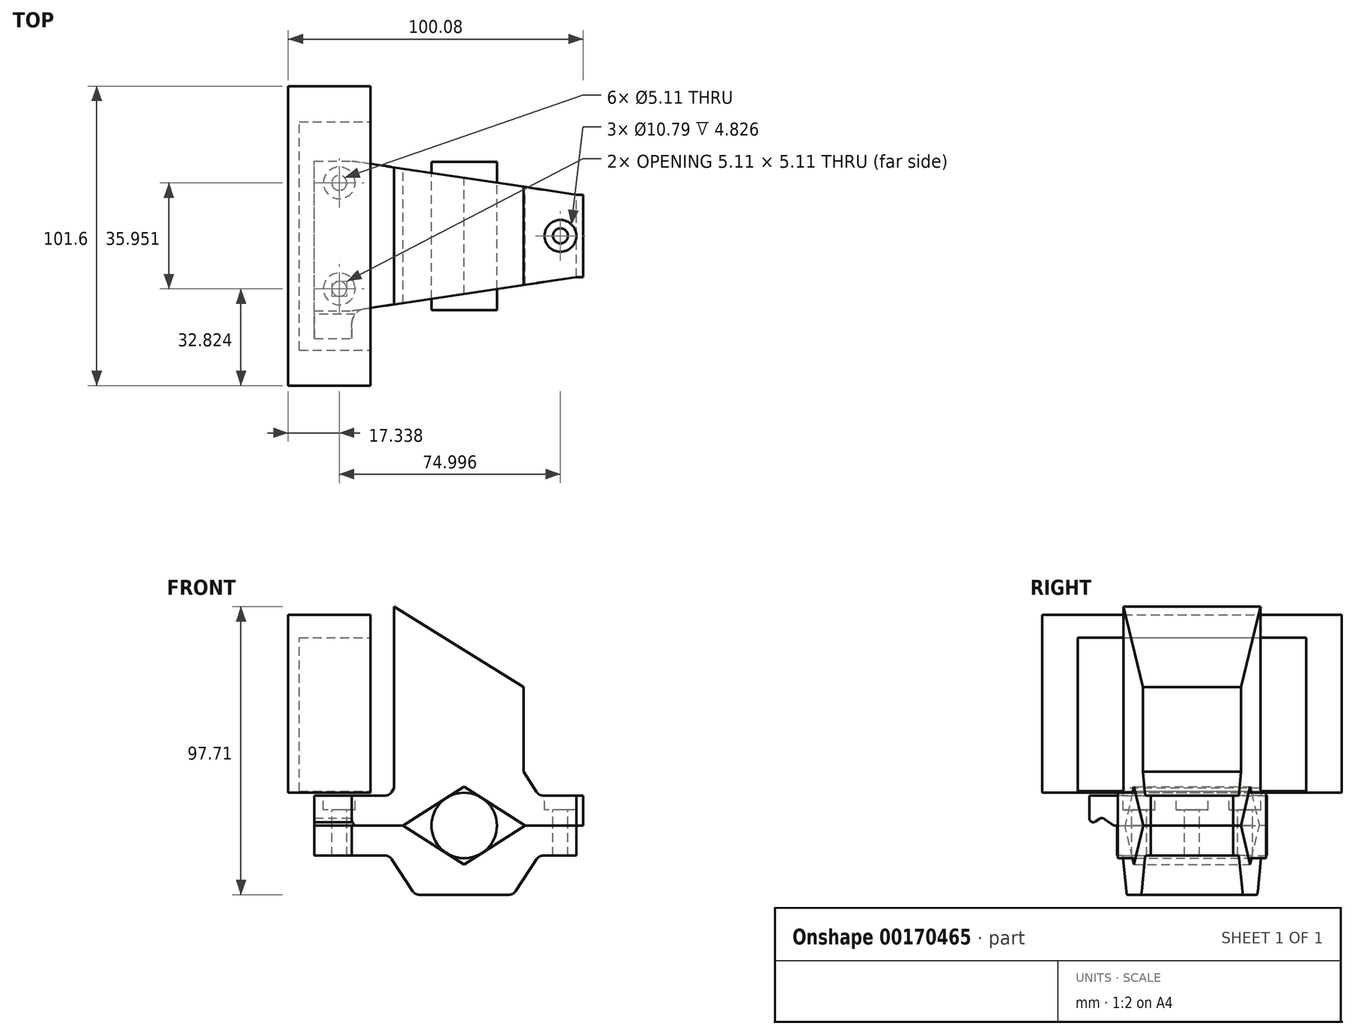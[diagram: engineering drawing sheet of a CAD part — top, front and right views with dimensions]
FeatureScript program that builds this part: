
annotation { "Feature Type Name" : "Feature", "Feature Type Description" : "" }
export const myFeature = defineFeature(function(context is Context, id is Id, definition is map)
    precondition{}
    {
        {
            var Q0;
            Q0=qCreatedBy(makeId("Front.planeOp"),FACE);
            var sketch = newSketch(context, id + "F0", { "sketchPlane" : qUnion([Q0])});
            skLineSegment(sketch, "E0", {"start": v(0, 0) * mm, "end": v(-38.1, 0) * mm});
            skLineSegment(sketch, "E1.MirrorCS", {"start": v(0, 0) * mm, "end": v(38.1, 0) * mm});
            skLineSegment(sketch, "E2", {"start": v(-38.1, 0) * mm, "end": v(-38.1, 10.16) * mm});
            skLineSegment(sketch, "E3", {"start": v(-38.1, 10.16) * mm, "end": v(-25.4, 10.16) * mm});
            skLineSegment(sketch, "E4", {"start": v(-25.4, 10.16) * mm, "end": v(-16.66, 23.43) * mm});
            skLineSegment(sketch, "E5", {"start": v(-16.66, 23.43) * mm, "end": v(0, 23.43) * mm});
            skLineSegment(sketch, "E6.MirrorCS", {"start": v(16.66, 23.43) * mm, "end": v(0, 23.43) * mm});
            skLineSegment(sketch, "E7.MirrorCS", {"start": v(25.4, 10.16) * mm, "end": v(16.66, 23.43) * mm});
            skLineSegment(sketch, "E8.MirrorCS", {"start": v(38.1, 10.16) * mm, "end": v(25.4, 10.16) * mm});
            skLineSegment(sketch, "E9.MirrorCS", {"start": v(38.1, 0) * mm, "end": v(38.1, 10.16) * mm});
            skSolve(sketch);
        }
        {
            var Q0;
            Q0=makeQuery(id+"F0.imprint","IMPRINT",FACE,{"disambiguationData":[TD([[makeQuery(id+"F0.imprint","IMPRINT",EDGE,{"derivedFrom":sQuery(id+"F0.wireOp",EDGE,"E0")}),-1.0]])]});
            extrude(context, id + "F1", {"entities" : qUnion([Q0]), "depth" : 50.8 * mm, "symmetric" : true});
        }
        {
            var Q0;
            Q0=makeQuery(id+"F1.opExtrude","SWEPT_EDGE",EDGE,{"disambiguationData":[OSD([sQuery(id+"F0.wireOp",EDGE,"E3"),sQuery(id+"F0.wireOp",EDGE,"E4")])]});
            var Q1;
            Q1=makeQuery(id+"F1.opExtrude","SWEPT_EDGE",EDGE,{"disambiguationData":[OSD([sQuery(id+"F0.wireOp",EDGE,"E4"),sQuery(id+"F0.wireOp",EDGE,"E5")])]});
            var Q2;
            Q2=makeQuery(id+"F1.opExtrude","SWEPT_EDGE",EDGE,{"disambiguationData":[OSD([sQuery(id+"F0.wireOp",EDGE,"E6.MirrorCS"),sQuery(id+"F0.wireOp",EDGE,"E7.MirrorCS")])]});
            var Q3;
            Q3=makeQuery(id+"F1.opExtrude","SWEPT_EDGE",EDGE,{"disambiguationData":[OSD([sQuery(id+"F0.wireOp",EDGE,"E7.MirrorCS"),sQuery(id+"F0.wireOp",EDGE,"E8.MirrorCS")])]});
            var Q4;
            Q4=makeQuery(id+"FDEMeBeCA99z51Q_1.boolean.opBoolean","COPY",EDGE,{"derivedFrom":makeQuery(id+"FDEMeBeCA99z51Q_1.opExtrude","SWEPT_EDGE",EDGE,{"disambiguationData":[OSD([sQuery(id+"FwCpyqjTZT8Y9rY_1.wireOp",EDGE,"hf3vtOHa-T0SD-jNCH-G6yt-N7PAPZoC1LBR"),sQuery(id+"FwCpyqjTZT8Y9rY_1.wireOp",EDGE,"xlTGKtzV-MVm6-p1pz-3OjP-4OK6CpVzw63G")])]})});
            var Q5;
            Q5=makeQuery(id+"FDEMeBeCA99z51Q_1.boolean.opBoolean","COPY",EDGE,{"derivedFrom":makeQuery(id+"FDEMeBeCA99z51Q_1.opExtrude","SWEPT_EDGE",EDGE,{"disambiguationData":[OSD([sQuery(id+"FwCpyqjTZT8Y9rY_1.wireOp",EDGE,"d345d4fc-93f9-48bb-a8d9-ec0b9a45d3b90.MirrorCS"),sQuery(id+"FwCpyqjTZT8Y9rY_1.wireOp",EDGE,"b8b2565e-5864-40b2-a50b-9c9d8fd83e460.MirrorCS")])]})});
            var Q6;
            Q6=makeQuery(id+"FDEMeBeCA99z51Q_1.boolean.opBoolean","COPY",EDGE,{"derivedFrom":makeQuery(id+"FDEMeBeCA99z51Q_1.opExtrude","SWEPT_EDGE",EDGE,{"disambiguationData":[OSD([sQuery(id+"FwCpyqjTZT8Y9rY_1.wireOp",EDGE,"5w3axiQP-sTHi-vBeq-NSh7-40wFJ7C5yblE"),sQuery(id+"FwCpyqjTZT8Y9rY_1.wireOp",EDGE,"hf3vtOHa-T0SD-jNCH-G6yt-N7PAPZoC1LBR")])]})});
            var Q7;
            Q7=makeQuery(id+"FDEMeBeCA99z51Q_1.boolean.opBoolean","COPY",EDGE,{"derivedFrom":makeQuery(id+"FDEMeBeCA99z51Q_1.opExtrude","SWEPT_EDGE",EDGE,{"disambiguationData":[OSD([sQuery(id+"FwCpyqjTZT8Y9rY_1.wireOp",EDGE,"b8b2565e-5864-40b2-a50b-9c9d8fd83e460.MirrorCS"),sQuery(id+"FwCpyqjTZT8Y9rY_1.wireOp",EDGE,"d29da1dd-462c-4873-ad7d-47c7f07a16380.MirrorCS")])]})});
            fillet(context, id + "F2", {"entities" : qUnion([Q0, Q1, Q2, Q3, Q4, Q5, Q6, Q7]), "radius" : 2.54 * mm, "tangentPropagation" : true, "allowEdgeOverflow" : false});
        }
        {
            var Q0;
            Q0=qCreatedBy(makeId("Top.planeOp"),FACE);
            var sketch = newSketch(context, id + "F3", { "sketchPlane" : qUnion([Q0])});
            skLineSegment(sketch, "E10", {"start": v(-38.1, -25.4) * mm, "end": v(38.1, -13.97) * mm});
            skLineSegment(sketch, "E11.0", {"start": v(-38.1, -25.4) * mm, "end": v(38.1, -25.4) * mm});
            skLineSegment(sketch, "E12.0", {"start": v(38.1, -25.4) * mm, "end": v(38.1, 25.4) * mm});
            skLineSegment(sketch, "E13.MirrorCS", {"start": v(38.1, 25.4) * mm, "end": v(38.1, -25.4) * mm});
            skLineSegment(sketch, "E14.MirrorCS", {"start": v(-38.1, 25.4) * mm, "end": v(38.1, 13.97) * mm});
            skLineSegment(sketch, "E15.MirrorCS", {"start": v(-38.1, 25.4) * mm, "end": v(38.1, 25.4) * mm});
            skSolve(sketch);
        }
        {
            var Q0;
            Q0=qSketchRegion(id+"F3",true);
            extrude(context, id + "F4", {"entities" : qUnion([Q0]), "operationType" : NewBodyOperationType.REMOVE, "depth" : 50.8 * mm});
        }
        {
            var Q0;
            Q0=qCreatedBy(makeId("Front.planeOp"),FACE);
            var sketch = newSketch(context, id + "F5", { "sketchPlane" : qUnion([Q0])});
            skCircle(sketch, "E16", {"center": v(0, 0) * mm, "radius": 11.11 * mm, "construction": true});
            skLineSegment(sketch, "E17", {"start": v(0, 0) * mm, "end": v(0, 13.18) * mm, "construction": true});
            skLineSegment(sketch, "E18", {"start": v(0, 13.18) * mm, "end": v(-20.68, 0) * mm});
            skLineSegment(sketch, "E19", {"start": v(0, 13.18) * mm, "end": v(20.68, 0) * mm});
            skLineSegment(sketch, "E20", {"start": v(-20.68, 0) * mm, "end": v(20.68, 0) * mm});
            skSolve(sketch);
        }
        {
            var Q0;
            Q0=qSketchRegion(id+"F5",true);
            extrude(context, id + "F6", {"entities" : qUnion([Q0]), "operationType" : NewBodyOperationType.REMOVE, "depth" : 63.5 * mm, "symmetric" : true});
        }
        {
            var Q0;
            Q0=qCreatedBy(makeId("Front.planeOp"),FACE);
            var sketch = newSketch(context, id + "F7", { "sketchPlane" : qUnion([Q0])});
            skCircle(sketch, "E21", {"center": v(0, 0) * mm, "radius": 11.11 * mm});
            skSolve(sketch);
        }
        {
            var Q0;
            Q0=makeQuery(id+"F7.imprint","IMPRINT",FACE,{"disambiguationData":[TD([[makeQuery(id+"F7.imprint","IMPRINT",EDGE,{"derivedFrom":sQuery(id+"F7.wireOp",EDGE,"E21")}),1.0]])]});
            extrude(context, id + "F8", {"entities" : qUnion([Q0]), "depth" : 50.3 * mm, "symmetric" : true});
        }
        {
            var Q0;
            Q0=makeQuery(id+"F1.opExtrude","SWEPT_FACE",FACE,{"disambiguationData":[OSD([sQuery(id+"F0.wireOp",EDGE,"E5"),sQuery(id+"F0.wireOp",EDGE,"E6.MirrorCS")])]});
            var sketch = newSketch(context, id + "F9", { "sketchPlane" : qUnion([Q0])});
            skLineSegment(sketch, "E22.right", {"start": v(20.1, 16.67) * mm, "end": v(20.1, -16.67) * mm});
            skPoint(sketch, "E23", {"position": v(20.1, 0) * mm});
            skLineSegment(sketch, "E24", {"start": v(20.1, 16.67) * mm, "end": v(-23.73, 23.24) * mm});
            skLineSegment(sketch, "E25", {"start": v(20.1, -16.67) * mm, "end": v(-23.73, -23.24) * mm});
            skLineSegment(sketch, "E26", {"start": v(-23.73, -23.24) * mm, "end": v(-23.73, 23.24) * mm});
            skSolve(sketch);
        }
        {
            var Q0;
            Q0=qCreatedBy(makeId("Right.planeOp"),FACE);
            cPlane(context, id + "F10", {"entities" : qUnion([Q0]), "cplaneType" : CPlaneType.OFFSET, "offset" : 31.75 * mm, "oppositeDirection" : true, "width" : 152.4 * mm, "height" : 152.4 * mm});
        }
        {
            var Q0;
            Q0=qCreatedBy(id+"F10.planeOp",FACE);
            var sketch = newSketch(context, id + "F11", { "sketchPlane" : qUnion([Q0])});
            skLineSegment(sketch, "E27.bottom", {"start": v(-38.73, 11.6) * mm, "end": v(38.74, 11.6) * mm});
            skLineSegment(sketch, "E27.top", {"start": v(-38.73, 63.67) * mm, "end": v(38.73, 63.67) * mm});
            skLineSegment(sketch, "E27.left", {"start": v(-38.73, 11.6) * mm, "end": v(-38.74, 63.67) * mm});
            skLineSegment(sketch, "E27.right", {"start": v(38.74, 11.6) * mm, "end": v(38.73, 63.67) * mm});
            skPoint(sketch, "E27.middle", {"position": v(0, 37.63) * mm});
            skSolve(sketch);
        }
        {
            var Q0;
            Q0=qCreatedBy(id+"F10.planeOp",FACE);
            var sketch = newSketch(context, id + "F12", { "sketchPlane" : qUnion([Q0])});
            skLineSegment(sketch, "E28.bottom", {"start": v(-50.8, 11.17) * mm, "end": v(50.8, 11.17) * mm});
            skLineSegment(sketch, "E28.top", {"start": v(-50.8, 71.5) * mm, "end": v(50.8, 71.5) * mm});
            skLineSegment(sketch, "E28.left", {"start": v(-50.8, 11.17) * mm, "end": v(-50.8, 71.5) * mm});
            skLineSegment(sketch, "E28.right", {"start": v(50.8, 11.17) * mm, "end": v(50.8, 71.5) * mm});
            skPoint(sketch, "E28.middle", {"position": v(0, 41.33) * mm});
            skSolve(sketch);
        }
        {
            var Q0;
            Q0=makeQuery(id+"F12.imprint","IMPRINT",FACE,{"disambiguationData":[TD([[makeQuery(id+"F12.imprint","IMPRINT",EDGE,{"derivedFrom":sQuery(id+"F12.wireOp",EDGE,"E28.bottom")}),1.0]])]});
            extrude(context, id + "F13", {"entities" : qUnion([Q0]), "operationType" : NewBodyOperationType.ADD, "oppositeDirection" : true, "depth" : 27.94 * mm});
        }
        {
            var Q0;
            Q0=makeQuery(id+"F11.imprint","IMPRINT",FACE,{"disambiguationData":[TD([[makeQuery(id+"F11.imprint","IMPRINT",EDGE,{"derivedFrom":sQuery(id+"F11.wireOp",EDGE,"E27.bottom")}),1.0]])]});
            extrude(context, id + "F14", {"entities" : qUnion([Q0]), "oppositeDirection" : true, "depth" : 24.13 * mm});
        }
        {
            var Q0;
            Q0=makeQuery(id+"F1.opExtrude","SWEPT_FACE",FACE,{"disambiguationData":[OSD([sQuery(id+"F0.wireOp",EDGE,"E2")])]});
            var sketch = newSketch(context, id + "F15", { "sketchPlane" : qUnion([Q0])});
            skLineSegment(sketch, "E29.0.0", {"start": v(-25.4, 10.16) * mm, "end": v(-25.4, 0) * mm});
            skLineSegment(sketch, "E29.0.1", {"start": v(-25.4, 0) * mm, "end": v(25.4, 0) * mm});
            skLineSegment(sketch, "E29.0.2", {"start": v(25.4, 0) * mm, "end": v(25.4, 10.16) * mm});
            skLineSegment(sketch, "E29.0.3", {"start": v(25.4, 10.16) * mm, "end": v(-25.4, 10.16) * mm});
            skSolve(sketch);
        }
        {
            var Q0;
            Q0=makeQuery(id+"F15.imprint","IMPRINT",FACE,{"disambiguationData":[TD([[makeQuery(id+"F15.imprint","IMPRINT",EDGE,{"derivedFrom":sQuery(id+"F15.wireOp",EDGE,"E29.0.0")}),-1.0]])]});
            extrude(context, id + "F16", {"entities" : qUnion([Q0]), "operationType" : NewBodyOperationType.ADD, "depth" : 12.7 * mm});
        }
        {
            var Q0;
            Q0=makeQuery(id+"F16.boolean.opBoolean","MERGE",FACE,{"derivedFrom":[makeQuery(id+"F6.boolean.opBoolean","SPLIT",FACE,{"disambiguationData":[TD([makeQuery(id+"F1.opExtrude","SWEPT_FACE",FACE,{"disambiguationData":[OSD([sQuery(id+"F0.wireOp",EDGE,"E2")])]})])],"derivedFrom":makeQuery(id+"F1.opExtrude","SWEPT_FACE",FACE,{"disambiguationData":[OSD([sQuery(id+"F0.wireOp",EDGE,"E0"),sQuery(id+"F0.wireOp",EDGE,"E1.MirrorCS")])]})}),makeQuery(id+"F16.opExtrude","SWEPT_FACE",FACE,{"disambiguationData":[OSD([sQuery(id+"F15.wireOp",EDGE,"E29.0.1")])]})]});
            cPlane(context, id + "F17", {"entities" : qUnion([Q0]), "cplaneType" : CPlaneType.OFFSET, "offset" : 0.03 * mm, "width" : 152.4 * mm, "height" : 152.4 * mm});
        }
        {
            var Q0;
            Q0=makeQuery(id+"F16.boolean.opBoolean","MERGE",FACE,{"derivedFrom":[makeQuery(id+"F1.opExtrude","SWEPT_FACE",FACE,{"disambiguationData":[OSD([sQuery(id+"F0.wireOp",EDGE,"E3")])]}),makeQuery(id+"F16.opExtrude","SWEPT_FACE",FACE,{"disambiguationData":[OSD([sQuery(id+"F15.wireOp",EDGE,"E29.0.3")])]})]});
            var sketch = newSketch(context, id + "F18", { "sketchPlane" : qUnion([Q0])});
            skLineSegment(sketch, "E30", {"start": v(-42.35, -17.98) * mm, "end": v(-42.35, 17.98) * mm, "construction": true});
            skPoint(sketch, "E31", {"position": v(-42.35, 0) * mm});
            skPoint(sketch, "E32", {"position": v(32.64, 0) * mm});
            skSolve(sketch);
        }
        {
            var Q0;
            Q0=sQuery(id+"F18.wireOp",VERTEX,"E30.end");
            var Q1;
            Q1=sQuery(id+"F18.wireOp",VERTEX,"E30.start");
            var Q2;
            Q2=sQuery(id+"F18.wireOp",VERTEX,"E32");
            var Q3;
            Q3=makeQuery(id+"F1.opExtrude","SWEPT_BODY",BODY,{"disambiguationData":[OSD([sQuery(id+"F0.wireOp",EDGE,"E0"),sQuery(id+"F0.wireOp",EDGE,"E1.MirrorCS"),sQuery(id+"F0.wireOp",EDGE,"E2"),sQuery(id+"F0.wireOp",EDGE,"E3"),sQuery(id+"F0.wireOp",EDGE,"E4"),sQuery(id+"F0.wireOp",EDGE,"E5"),sQuery(id+"F0.wireOp",EDGE,"E6.MirrorCS"),sQuery(id+"F0.wireOp",EDGE,"E7.MirrorCS"),sQuery(id+"F0.wireOp",EDGE,"E8.MirrorCS"),sQuery(id+"F0.wireOp",EDGE,"E9.MirrorCS")])]});
            hole(context, id + "F19", {"style" : HoleStyle.SIMPLE, "endStyle" : HoleEndStyle.THROUGH, "standardTappedOrClearance" : lookupTablePath({ "standard" : "ANSI", "fit" : "Normal (ASME)", "size" : "#1", "type" : "Clearance" }), "standardBlindInLast" : lookupTablePath({ "fit" : "Free", "standard" : "ANSI", "size" : "#1", "type" : "Clearance" }), "holeDiameter" : 2.06 * mm, "locations" : qUnion([Q0, Q1, Q2]), "scope" : qUnion([Q3]), "isTappedThrough" : true});
        }
        {
            var Q0;
            Q0=makeQuery(id+"F1.opExtrude","SWEPT_BODY",BODY,{"disambiguationData":[OSD([sQuery(id+"F0.wireOp",EDGE,"E0"),sQuery(id+"F0.wireOp",EDGE,"E1.MirrorCS"),sQuery(id+"F0.wireOp",EDGE,"E2"),sQuery(id+"F0.wireOp",EDGE,"E3"),sQuery(id+"F0.wireOp",EDGE,"E4"),sQuery(id+"F0.wireOp",EDGE,"E5"),sQuery(id+"F0.wireOp",EDGE,"E6.MirrorCS"),sQuery(id+"F0.wireOp",EDGE,"E7.MirrorCS"),sQuery(id+"F0.wireOp",EDGE,"E8.MirrorCS"),sQuery(id+"F0.wireOp",EDGE,"E9.MirrorCS")])]});
            var Q1;
            Q1=qCreatedBy(id+"F17.planeOp",FACE);
            mirror(context, id + "F20", {"operationType" : NewBodyOperationType.ADD, "entities" : qUnion([Q0]), "mirrorPlane" : qUnion([Q1])});
        }
        {
            var Q0;
            Q0=makeQuery(id+"F16.boolean.opBoolean","MERGE",FACE,{"derivedFrom":[makeQuery(id+"F1.opExtrude","SWEPT_FACE",FACE,{"disambiguationData":[OSD([sQuery(id+"F0.wireOp",EDGE,"E3")])]}),makeQuery(id+"F16.opExtrude","SWEPT_FACE",FACE,{"disambiguationData":[OSD([sQuery(id+"F15.wireOp",EDGE,"E29.0.3")])]})]});
            var sketch = newSketch(context, id + "F21", { "sketchPlane" : qUnion([Q0])});
            skPoint(sketch, "E33", {"position": v(-42.35, 17.98) * mm});
            skPoint(sketch, "E34", {"position": v(-42.35, -17.98) * mm});
            skSolve(sketch);
        }
        {
            var Q0;
            Q0=makeQuery(id+"F1.opExtrude","SWEPT_FACE",FACE,{"disambiguationData":[OSD([sQuery(id+"F0.wireOp",EDGE,"E8.MirrorCS")])]});
            var sketch = newSketch(context, id + "F22", { "sketchPlane" : qUnion([Q0])});
            skPoint(sketch, "E35", {"position": v(32.64, 0) * mm});
            skSolve(sketch);
        }
        {
            var Q0;
            Q0=sQuery(id+"F21.wireOp",VERTEX,"E33");
            var Q1;
            Q1=sQuery(id+"F21.wireOp",VERTEX,"E34");
            var Q2;
            Q2=sQuery(id+"F22.wireOp",VERTEX,"E35");
            var Q3;
            Q3=makeQuery(id+"F1.opExtrude","SWEPT_BODY",BODY,{"disambiguationData":[OSD([sQuery(id+"F0.wireOp",EDGE,"E0"),sQuery(id+"F0.wireOp",EDGE,"E1.MirrorCS"),sQuery(id+"F0.wireOp",EDGE,"E2"),sQuery(id+"F0.wireOp",EDGE,"E3"),sQuery(id+"F0.wireOp",EDGE,"E4"),sQuery(id+"F0.wireOp",EDGE,"E5"),sQuery(id+"F0.wireOp",EDGE,"E6.MirrorCS"),sQuery(id+"F0.wireOp",EDGE,"E7.MirrorCS"),sQuery(id+"F0.wireOp",EDGE,"E8.MirrorCS"),sQuery(id+"F0.wireOp",EDGE,"E9.MirrorCS")])]});
            var Q4;
            Q4=makeQuery(id+"F20.opPattern","COPY",BODY,{"derivedFrom":makeQuery(id+"F1.opExtrude","SWEPT_BODY",BODY,{"disambiguationData":[OSD([sQuery(id+"F0.wireOp",EDGE,"E0"),sQuery(id+"F0.wireOp",EDGE,"E1.MirrorCS"),sQuery(id+"F0.wireOp",EDGE,"E2"),sQuery(id+"F0.wireOp",EDGE,"E3"),sQuery(id+"F0.wireOp",EDGE,"E4"),sQuery(id+"F0.wireOp",EDGE,"E5"),sQuery(id+"F0.wireOp",EDGE,"E6.MirrorCS"),sQuery(id+"F0.wireOp",EDGE,"E7.MirrorCS"),sQuery(id+"F0.wireOp",EDGE,"E8.MirrorCS"),sQuery(id+"F0.wireOp",EDGE,"E9.MirrorCS")])]}),"instanceName":"1"});
            hole(context, id + "F23", {"style" : HoleStyle.C_BORE, "endStyle" : HoleEndStyle.THROUGH, "holeDiameter" : 5.1 * mm, "cBoreDiameter" : 10.8 * mm, "cBoreDepth" : 4.83 * mm, "locations" : qUnion([Q0, Q1, Q2]), "scope" : qUnion([Q3, Q4]), "isTappedThrough" : true});
        }
        {
            var Q0;
            Q0 = qSketchRegion(id + "F9", true);
            extrude(context, id + "F24", {"entities" : qUnion([Q0]), "operationType" : NewBodyOperationType.ADD, "depth" : 50.8 * mm, "hasSecondDirection" : true, "secondDirectionBound" : BoundingType.UP_TO_NEXT, "secondDirectionOppositeDirection" : true, "secondDirectionDepth" : 25.4 * mm});
        }
        {
            var Q0;
            Q0=qCreatedBy(makeId("Front.planeOp"),FACE);
            var sketch = newSketch(context, id + "F25", { "sketchPlane" : qUnion([Q0])});
            skLineSegment(sketch, "E36", {"start": v(-23.73, 74.23) * mm, "end": v(20.1, 46.9) * mm});
            skLineSegment(sketch, "E37.0", {"start": v(20.1, 74.23) * mm, "end": v(-23.73, 74.23) * mm});
            skLineSegment(sketch, "E38.0", {"start": v(20.1, 74.23) * mm, "end": v(20.1, 46.9) * mm});
            skPoint(sketch, "E39.orphan", {"position": v(20.1, 18.2) * mm});
            skSolve(sketch);
        }
        {
            var Q0;
            Q0 = qSketchRegion(id + "F25", true);
            extrude(context, id + "F26", {"entities" : qUnion([Q0]), "operationType" : NewBodyOperationType.REMOVE, "oppositeDirection" : true, "depth" : 106.17 * mm, "symmetric" : true});
        }
        {
            var Q0;
            Q0=makeQuery(id+"F16.opExtrude","SWEPT_FACE",FACE,{"disambiguationData":[OSD([sQuery(id+"F15.wireOp",EDGE,"E29.0.2")])]});
            extrude(context, id + "F27", {"entities" : qUnion([Q0]), "depth" : 9.4 * mm});
        }
        {
            var Q0;
            {var subQ0=sQuery(id+"F15.wireOp",EDGE,"E29.0.2");Q0=makeQuery(id+"F27.boolean.opBoolean","MERGE",FACE,{"derivedFrom":[makeQuery(id+"F16.opExtrude","CAP_FACE",FACE,{"disambiguationData":[OSD([sQuery(id+"F15.wireOp",EDGE,"E29.0.0"),sQuery(id+"F15.wireOp",EDGE,"E29.0.1"),subQ0,sQuery(id+"F15.wireOp",EDGE,"E29.0.3")])],"isStart":false}),makeQuery(id+"F27.opExtrude","SWEPT_FACE",FACE,{"disambiguationData":[OSD([subQ0])]})]});}
            var sketch = newSketch(context, id + "F28", { "sketchPlane" : qUnion([Q0])});
            skLineSegment(sketch, "E40", {"start": v(26.58, 0) * mm, "end": v(30.6, 2.8) * mm});
            skLineSegment(sketch, "E41", {"start": v(30.6, 2.8) * mm, "end": v(34.8, 0) * mm});
            skLineSegment(sketch, "E42", {"start": v(34.8, 0) * mm, "end": v(26.58, 0) * mm});
            skSolve(sketch);
        }
        {
            var Q0;
            Q0=makeQuery(id+"F28.imprint","IMPRINT",FACE,{"disambiguationData":[TD([[makeQuery(id+"F28.imprint","IMPRINT",EDGE,{"derivedFrom":sQuery(id+"F28.wireOp",EDGE,"E40")}),-1.0]])]});
            extrude(context, id + "F29", {"entities" : qUnion([Q0]), "operationType" : NewBodyOperationType.REMOVE, "oppositeDirection" : true, "depth" : 25.4 * mm});
        }
        {
            var Q0;
            Q0=makeQuery(id+"F29.boolean.opBoolean","COPY",EDGE,{"derivedFrom":makeQuery(id+"F29.opExtrude","SWEPT_EDGE",EDGE,{"disambiguationData":[OSD([sQuery(id+"F28.wireOp",EDGE,"E40"),sQuery(id+"F28.wireOp",EDGE,"E41")])]})});
            var Q1;
            {var subQ0=sQuery(id+"F15.wireOp",EDGE,"E29.0.2");Q1=makeQuery(id+"F29.boolean.opBoolean","MERGE",EDGE,{"derivedFrom":[makeQuery(id+"F27.opExtrude","CAP_EDGE",EDGE,{"disambiguationData":[OSD([sQuery(id+"F15.wireOp",EDGE,"E29.0.1"),subQ0])],"isStart":false}),makeQuery(id+"F29.opExtrude","SWEPT_EDGE",EDGE,{"disambiguationData":[OSD([subQ0,sQuery(id+"F28.wireOp",EDGE,"E41"),sQuery(id+"F28.wireOp",EDGE,"E42")])]})]});}
            var Q2;
            Q2=makeQuery(id+"F29.boolean.opBoolean","COPY",EDGE,{"derivedFrom":makeQuery(id+"F29.opExtrude","SWEPT_EDGE",EDGE,{"disambiguationData":[OSD([sQuery(id+"F15.wireOp",EDGE,"E29.0.1"),sQuery(id+"F15.wireOp",EDGE,"E29.0.2"),sQuery(id+"F28.wireOp",EDGE,"E40"),sQuery(id+"F28.wireOp",EDGE,"E42")])]})});
            fillet(context, id + "F30", {"entities" : qUnion([Q0, Q1, Q2]), "radius" : 1.27 * mm, "tangentPropagation" : true, "allowEdgeOverflow" : false});
        }
        {
            var Q0;
            Q0=makeQuery(id+"F3vK7hlCNSFnxgN_4.1.F27.opExtrude","SWEPT_BODY",BODY,{"disambiguationData":[OSD([sQuery(id+"F15.wireOp",EDGE,"E29.0.2")])]});
            var Q1;
            Q1=makeQuery(id+"F1.opExtrude","SWEPT_BODY",BODY,{"disambiguationData":[OSD([sQuery(id+"F0.wireOp",EDGE,"E0"),sQuery(id+"F0.wireOp",EDGE,"E1.MirrorCS"),sQuery(id+"F0.wireOp",EDGE,"E2"),sQuery(id+"F0.wireOp",EDGE,"E3"),sQuery(id+"F0.wireOp",EDGE,"E4"),sQuery(id+"F0.wireOp",EDGE,"E5"),sQuery(id+"F0.wireOp",EDGE,"E6.MirrorCS"),sQuery(id+"F0.wireOp",EDGE,"E7.MirrorCS"),sQuery(id+"F0.wireOp",EDGE,"E8.MirrorCS"),sQuery(id+"F0.wireOp",EDGE,"E9.MirrorCS")])]});
            var Q2;
            Q2=makeQuery(id+"F27.opExtrude","SWEPT_BODY",BODY,{"disambiguationData":[OSD([sQuery(id+"F15.wireOp",EDGE,"E29.0.2")])]});
            booleanBodies(context, id + "F31", {"operationType" : BooleanOperationType.UNION, "tools" : qUnion([Q0, Q1, Q2])});
        }
        {
            var Q0;
            {var subQ0=sQuery(id+"F15.wireOp",EDGE,"E29.0.2");var subQ1=sQuery(id+"F3.wireOp",EDGE,"E11.0");var subQ2=sQuery(id+"F3.wireOp",EDGE,"E10");var subQ3=sQuery(id+"F0.wireOp",EDGE,"E2");Q0=makeQuery(id+"F31.opBoolean","MERGE",EDGE,{"derivedFrom":[makeQuery(id+"F16.boolean.opBoolean","MERGE",EDGE,{"derivedFrom":[makeQuery(id+"F4.boolean.opBoolean","MERGE",EDGE,{"derivedFrom":[makeQuery(id+"F1.opExtrude","CAP_EDGE",EDGE,{"disambiguationData":[OSD([subQ3])],"isStart":false}),makeQuery(id+"F4.opExtrude","SWEPT_EDGE",EDGE,{"disambiguationData":[OSD([subQ2,subQ1])]})]}),makeQuery(id+"F16.opExtrude","CAP_EDGE",EDGE,{"disambiguationData":[OSD([subQ0])],"isStart":true})]}),makeQuery(id+"F27.opExtrude","CAP_EDGE",EDGE,{"disambiguationData":[OSD([subQ3,subQ2,subQ1,subQ0])],"isStart":true})]});}
            var Q1;
            {var subQ0=sQuery(id+"F0.wireOp",EDGE,"E2");Q1=makeQuery(id+"F31.opBoolean","MERGE",EDGE,{"derivedFrom":[makeQuery(id+"F16.boolean.opBoolean","MERGE",EDGE,{"derivedFrom":[makeQuery(id+"F4.boolean.opBoolean","MERGE",EDGE,{"derivedFrom":[makeQuery(id+"F1.opExtrude","CAP_EDGE",EDGE,{"disambiguationData":[OSD([subQ0])],"isStart":true}),makeQuery(id+"F4.opExtrude","SWEPT_EDGE",EDGE,{"disambiguationData":[OSD([sQuery(id+"F3.wireOp",EDGE,"E14.MirrorCS"),sQuery(id+"F3.wireOp",EDGE,"E15.MirrorCS")])]})]}),makeQuery(id+"F16.opExtrude","CAP_EDGE",EDGE,{"disambiguationData":[OSD([sQuery(id+"F15.wireOp",EDGE,"E29.0.0")])],"isStart":true})]}),makeQuery(id+"F3vK7hlCNSFnxgN_4.1.F27.opExtrude","CAP_EDGE",EDGE,{"disambiguationData":[OSD([subQ0,sQuery(id+"F3.wireOp",EDGE,"E10"),sQuery(id+"F3.wireOp",EDGE,"E11.0"),sQuery(id+"F15.wireOp",EDGE,"E29.0.2")])],"isStart":true})]});}
            fillet(context, id + "F32", {"entities" : qUnion([Q0, Q1]), "radius" : 5.08 * mm, "tangentPropagation" : true, "allowEdgeOverflow" : false});
        }
        {
            var Q0;
            Q0=makeQuery(id+"F24.boolean.opBoolean","MERGE",FACE,{"derivedFrom":[makeQuery(id+"F4.boolean.opBoolean","COPY",FACE,{"derivedFrom":makeQuery(id+"F4.opExtrude","SWEPT_FACE",FACE,{"disambiguationData":[OSD([sQuery(id+"F3.wireOp",EDGE,"E10")])]})}),makeQuery(id+"F24.opExtrude","SWEPT_FACE",FACE,{"disambiguationData":[OSD([sQuery(id+"F9.wireOp",EDGE,"E25")])]})]});
            var sketch = newSketch(context, id + "F33", { "sketchPlane" : qUnion([Q0])});
            skCircle(sketch, "E43", {"center": v(-5.34, 37.72) * mm, "radius": 12.7 * mm});
            skLineSegment(sketch, "E44", {"start": v(-5.34, 38.99) * mm, "end": v(-5.34, 36.45) * mm, "construction": true});
            skArc(sketch, "E45", {"start": v(-15.58, 36.45) * mm, "mid": v(-5.34, 27.4) * mm, "end": v(4.89, 36.45) * mm});
            skLineSegment(sketch, "E46", {"start": v(-15.58, 38.99) * mm, "end": v(4.89, 38.99) * mm});
            skLineSegment(sketch, "E47", {"start": v(-5.34, 36.45) * mm, "end": v(-15.58, 36.45) * mm});
            skLineSegment(sketch, "E48", {"start": v(-5.34, 36.45) * mm, "end": v(4.89, 36.45) * mm});
            skArc(sketch, "E49.trimOffspring", {"start": v(4.89, 38.99) * mm, "mid": v(-5.34, 48.02) * mm, "end": v(-15.58, 38.99) * mm});
            skSolve(sketch);
        }
        {
            var Q0;
            Q0=makeQuery(id+"F1.opExtrude","SWEPT_FACE",FACE,{"disambiguationData":[OSD([sQuery(id+"F0.wireOp",EDGE,"E9.MirrorCS")])]});
            extrude(context, id + "F34", {"entities" : qUnion([Q0]), "operationType" : NewBodyOperationType.ADD, "depth" : 2.3 * mm});
        }
    });
